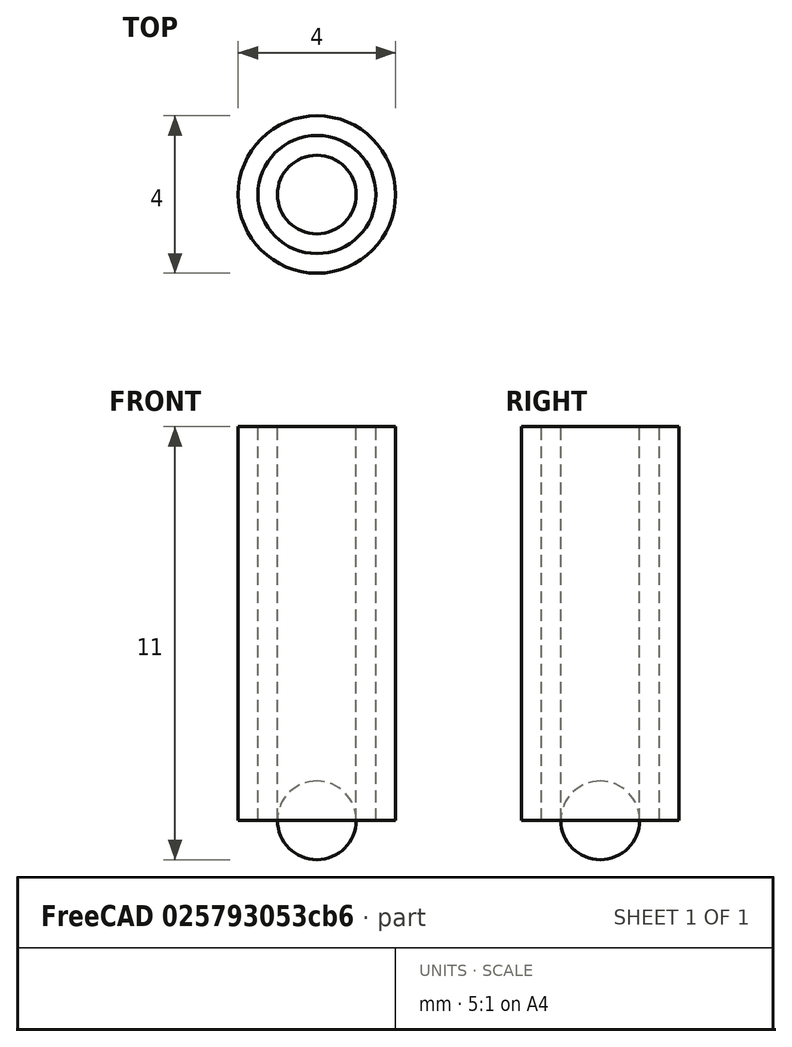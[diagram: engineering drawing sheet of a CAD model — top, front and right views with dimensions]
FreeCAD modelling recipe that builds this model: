
FCSTD DOCUMENT  (FreeCAD 0.19R)
Label: ikpy
License: All rights reserved
LicenseURL: http://en.wikipedia.org/wiki/All_rights_reserved
objects: App::Part×4, Part::Cylinder×3, App::DocumentObjectGroup×2, App::Placement×1, App::FeaturePython×1, Part::Sphere×1
note: 4 computed .brp shape members not serialized (recipe doc carries the construction recipe); baked Part::Feature solids carry a one-line shape summary decoded from their .brp

FEATURE [Part::Cylinder] Cylinder  label="Cylindre"
  Angle = 360
  AttacherType = Attacher::AttachEngine3D
  Height = 10
  Radius = 2
FEATURE [App::Part] Part  label="Arm1"
  Group = -> [Cylinder]
  Origin = -> Origin
  Placement = pos=(0,0,0) rot=(0,0,1;0.463654rad)
FEATURE [Part::Cylinder] Cylinder001  label="Cylindre001"
  Angle = 360
  AttacherType = Attacher::AttachEngine3D
  Height = 10
  Radius = 1.5
FEATURE [App::Part] Part001  label="Arm2"
  Group = -> [Cylinder001]
  Origin = -> Origin001
  Placement = pos=(0,0,10) rot=(0.180872,-0.766176,0.616652;0.73123rad)
FEATURE [Part::Cylinder] Cylinder002  label="Cylindre002"
  Angle = 360
  AttacherType = Attacher::AttachEngine3D
  Height = 10
  Radius = 1
FEATURE [App::Part] Part002  label="Arm3"
  Group = -> [Cylinder002]
  Origin = -> Origin002
  Placement = pos=(-4.83127,-2.4157,18.4157) rot=(-0.221837,0.939706,0.260272;1.47336rad)
FEATURE [App::Placement] Target
  Placement = pos=(4,2,20) rot=(0,0,1;0rad)
FEATURE [App::FeaturePython] PDInclude001  label="PDInclude"  # WARN: FeaturePython — macro-defined, semantics opaque (R4)
FEATURE [Part::Sphere] Sphere  label="Sphère"
  Angle1 = -90
  Angle2 = 90
  Angle3 = 360
  AttacherType = Attacher::AttachEngine3D
  Radius = 1
FEATURE [App::Part] Part003  label="Hand"
  Group = -> [Sphere]
  Origin = -> Origin003
  Placement = pos=(4,2,20) rot=(-0.221837,0.939706,0.260272;1.47336rad)
FEATURE [App::DocumentObjectGroup] Group  label="Controler"
  Group = -> [PDInclude001,Target]
FEATURE [App::DocumentObjectGroup] Group001  label="Robot"
  Group = -> [Part,Part001,Part002,Part003]
